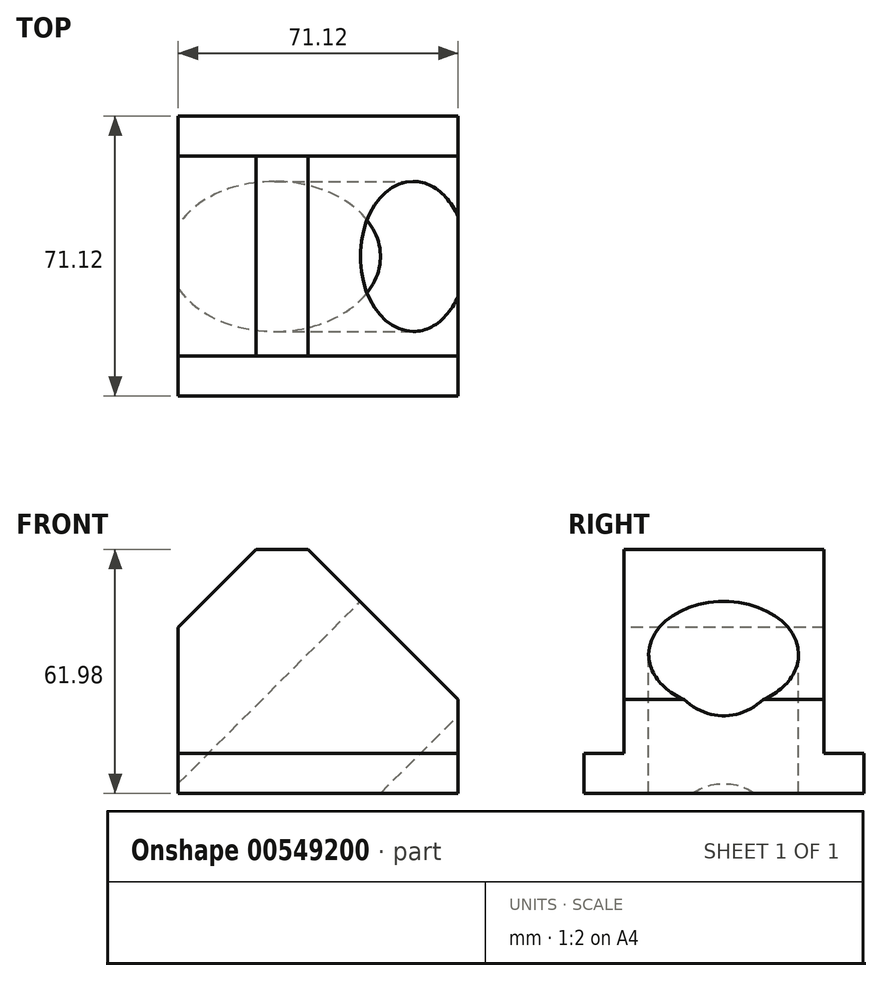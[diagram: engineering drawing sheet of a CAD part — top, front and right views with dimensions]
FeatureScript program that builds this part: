
annotation { "Feature Type Name" : "Feature", "Feature Type Description" : "" }
export const myFeature = defineFeature(function(context is Context, id is Id, definition is map)
    precondition{}
    {
        {
            var Q0;
            Q0=qCreatedBy(makeId("Top.planeOp"),FACE);
            var sketch = newSketch(context, id + "F0", { "sketchPlane" : qUnion([Q0])});
            skLineSegment(sketch, "E0.bottom", {"start": v(-17.96, -40.14) * mm, "end": v(53.16, -40.14) * mm});
            skLineSegment(sketch, "E0.top", {"start": v(-17.96, 30.98) * mm, "end": v(53.16, 30.98) * mm});
            skLineSegment(sketch, "E0.left", {"start": v(-17.96, -40.14) * mm, "end": v(-17.96, 30.98) * mm});
            skLineSegment(sketch, "E0.right", {"start": v(53.16, -40.14) * mm, "end": v(53.16, 30.98) * mm});
            skSolve(sketch);
        }
        {
            var Q0;
            Q0=makeQuery(id+"F0.imprint","IMPRINT",FACE,{"disambiguationData":[TD([[makeQuery(id+"F0.imprint","IMPRINT",EDGE,{"derivedFrom":sQuery(id+"F0.wireOp",EDGE,"E0.bottom")}),1.0]])]});
            extrude(context, id + "F1", {"entities" : qUnion([Q0]), "depth" : 10.16 * mm, "offsetDistance" : 25.4 * mm});
        }
        {
            var Q0;
            Q0=makeQuery(id+"F1.opExtrude","CAP_FACE",FACE,{"disambiguationData":[OSD([sQuery(id+"F0.wireOp",EDGE,"E0.bottom"),sQuery(id+"F0.wireOp",EDGE,"E0.top"),sQuery(id+"F0.wireOp",EDGE,"E0.left"),sQuery(id+"F0.wireOp",EDGE,"E0.right")])],"isStart":false});
            var sketch = newSketch(context, id + "F2", { "sketchPlane" : qUnion([Q0])});
            skPoint(sketch, "E1", {"position": v(53.16, -29.98) * mm});
            skPoint(sketch, "E2", {"position": v(-17.96, -29.98) * mm});
            skLineSegment(sketch, "E3", {"start": v(-17.96, -29.98) * mm, "end": v(53.16, -29.98) * mm});
            skPoint(sketch, "E4", {"position": v(53.16, 20.82) * mm});
            skPoint(sketch, "E5", {"position": v(-17.96, 20.82) * mm});
            skLineSegment(sketch, "E6", {"start": v(-17.96, 20.82) * mm, "end": v(53.16, 20.82) * mm});
            skSolve(sketch);
        }
        {
            var Q0;
            {var subQ0=sQuery(id+"F2.wireOp",EDGE,"E3");Q0=makeQuery(id+"F2.imprint","IMPRINT",FACE,{"disambiguationData":[TD([[makeQuery(id+"F2.imprint","IMPRINT",EDGE,{"derivedFrom":subQ0}),1.0]])]});}
            extrude(context, id + "F3", {"entities" : qUnion([Q0]), "operationType" : NewBodyOperationType.ADD, "depth" : 51.82 * mm, "offsetDistance" : 25.4 * mm});
        }
        {
            var Q0;
            Q0=makeQuery(id+"F3.opExtrude","SWEPT_FACE",FACE,{"disambiguationData":[OSD([sQuery(id+"F2.wireOp",EDGE,"E3")])]});
            var sketch = newSketch(context, id + "F4", { "sketchPlane" : qUnion([Q0])});
            skPoint(sketch, "E7", {"position": v(1.87, 61.98) * mm});
            skPoint(sketch, "E8", {"position": v(-17.96, 42.15) * mm});
            skLineSegment(sketch, "E9", {"start": v(-17.96, 42.15) * mm, "end": v(1.87, 61.98) * mm});
            skSolve(sketch);
        }
        {
            var Q0;
            {var subQ0=sQuery(id+"F4.wireOp",EDGE,"E9");Q0=makeQuery(id+"F4.imprint","IMPRINT",FACE,{"disambiguationData":[TD([[makeQuery(id+"F4.imprint","IMPRINT",EDGE,{"derivedFrom":subQ0}),1.0]])]});}
            extrude(context, id + "F5", {"entities" : qUnion([Q0]), "operationType" : NewBodyOperationType.REMOVE, "oppositeDirection" : true, "depth" : 71.12 * mm, "offsetDistance" : 25.4 * mm});
        }
        {
            var Q0;
            Q0=makeQuery(id+"F3.opExtrude","SWEPT_FACE",FACE,{"disambiguationData":[OSD([sQuery(id+"F2.wireOp",EDGE,"E3")])]});
            var sketch = newSketch(context, id + "F6", { "sketchPlane" : qUnion([Q0])});
            skPoint(sketch, "E10", {"position": v(53.16, 23.88) * mm});
            skLineSegment(sketch, "E11", {"start": v(53.16, 23.88) * mm, "end": v(15.06, 61.98) * mm});
            skSolve(sketch);
        }
        {
            var Q0;
            {var subQ0=sQuery(id+"F6.wireOp",EDGE,"E11");Q0=makeQuery(id+"F6.imprint","IMPRINT",FACE,{"disambiguationData":[TD([[makeQuery(id+"F6.imprint","IMPRINT",EDGE,{"derivedFrom":subQ0}),-1.0]])]});}
            extrude(context, id + "F7", {"entities" : qUnion([Q0]), "operationType" : NewBodyOperationType.REMOVE, "oppositeDirection" : true, "depth" : 71.12 * mm, "offsetDistance" : 25.4 * mm});
        }
        {
            var Q0;
            Q0=makeQuery(id+"F7.boolean.opBoolean","COPY",FACE,{"derivedFrom":makeQuery(id+"F7.opExtrude","SWEPT_FACE",FACE,{"disambiguationData":[OSD([sQuery(id+"F6.wireOp",EDGE,"E11")])]})});
            var sketch = newSketch(context, id + "F8", { "sketchPlane" : qUnion([Q0])});
            skPoint(sketch, "E12", {"position": v(-4.7, -4.58) * mm});
            skPoint(sketch, "E12.positionSnap0", {"position": v(-33.17, -4.58) * mm});
            skCircle(sketch, "E13", {"center": v(-4.7, -4.58) * mm, "radius": 19.05 * mm});
            skSolve(sketch);
        }
        {
            var Q0;
            Q0=makeQuery(id+"F8.imprint","IMPRINT",FACE,{"disambiguationData":[TD([[makeQuery(id+"F8.imprint","IMPRINT",EDGE,{"derivedFrom":sQuery(id+"F8.wireOp",EDGE,"E13")}),1.0]])]});
            extrude(context, id + "F9", {"entities" : qUnion([Q0]), "operationType" : NewBodyOperationType.REMOVE, "oppositeDirection" : true, "depth" : 101.6 * mm, "offsetDistance" : 25.4 * mm});
        }
    });
